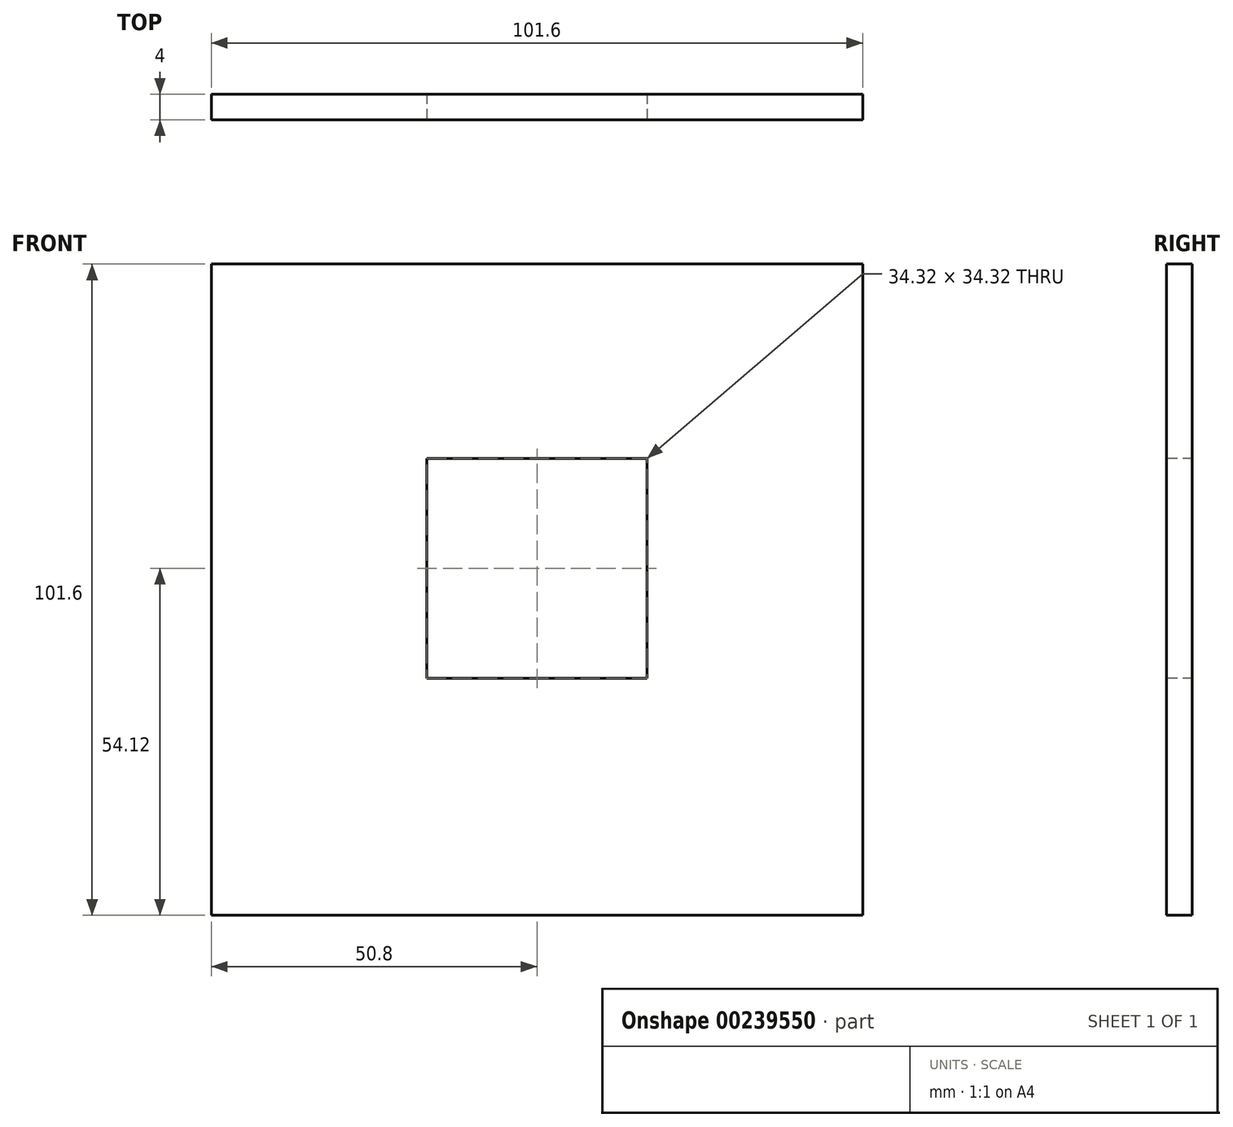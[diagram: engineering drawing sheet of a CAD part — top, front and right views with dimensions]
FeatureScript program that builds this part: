
annotation { "Feature Type Name" : "Feature", "Feature Type Description" : "" }
export const myFeature = defineFeature(function(context is Context, id is Id, definition is map)
    precondition{}
    {
        {
            assignVariable(context, id + "F0", {"name" : "L", "anyValue" : 4});
        }
        {
            var Q0;
            Q0=qCreatedBy(makeId("Front.planeOp"),FACE);
            var sketch = newSketch(context, id + "F1", { "sketchPlane" : qUnion([Q0])});
            skLineSegment(sketch, "E0.bottom", {"start": v(50.8, 50.8) * mm, "end": v(-50.8, 50.8) * mm});
            skLineSegment(sketch, "E0.top", {"start": v(50.8, -50.8) * mm, "end": v(-50.8, -50.8) * mm});
            skLineSegment(sketch, "E0.left", {"start": v(50.8, 50.8) * mm, "end": v(50.8, -50.8) * mm});
            skLineSegment(sketch, "E0.right", {"start": v(-50.8, 50.8) * mm, "end": v(-50.8, -50.8) * mm});
            skPoint(sketch, "E0.middle", {"position": v(0, 0) * mm});
            skSolve(sketch);
        }
        {
            var Q0;
            Q0=makeQuery(id+"F1.imprint","IMPRINT",FACE,{"disambiguationData":[TD([[makeQuery(id+"F1.imprint","IMPRINT",EDGE,{"derivedFrom":sQuery(id+"F1.wireOp",EDGE,"E0.bottom")}),1.0]])]});
            extrude(context, id + "F2", {"entities" : qUnion([Q0]), "endBound" : BoundingType.SYMMETRIC, "depth" : (getVariable(context, 'L')) * mm});
        }
        {
            var Q0;
            Q0=makeQuery(id+"F2.opExtrude","CAP_FACE",FACE,{"disambiguationData":[OSD([sQuery(id+"F1.wireOp",EDGE,"E0.bottom"),sQuery(id+"F1.wireOp",EDGE,"E0.top"),sQuery(id+"F1.wireOp",EDGE,"E0.left"),sQuery(id+"F1.wireOp",EDGE,"E0.right")])],"isStart":false});
            var sketch = newSketch(context, id + "F3", { "sketchPlane" : qUnion([Q0])});
            skLineSegment(sketch, "E1.bottom", {"start": v(17.16, 20.48) * mm, "end": v(-17.16, 20.48) * mm});
            skLineSegment(sketch, "E1.top", {"start": v(17.16, -13.84) * mm, "end": v(-17.16, -13.84) * mm});
            skLineSegment(sketch, "E1.left", {"start": v(17.16, 20.48) * mm, "end": v(17.16, -13.84) * mm});
            skLineSegment(sketch, "E1.right", {"start": v(-17.16, 20.48) * mm, "end": v(-17.16, -13.84) * mm});
            skPoint(sketch, "E1.middle", {"position": v(0, 3.32) * mm});
            skSolve(sketch);
        }
        {
            var Q0;
            Q0 = qSketchRegion(id + "F3", true);
            extrude(context, id + "F4", {"entities" : qUnion([Q0]), "operationType" : NewBodyOperationType.REMOVE, "oppositeDirection" : true, "depth" : 46.23 * mm});
        }
        {
            var Q0;
            Q0=makeQuery(id+"F2.opExtrude","CAP_FACE",FACE,{"disambiguationData":[OSD([sQuery(id+"F1.wireOp",EDGE,"E0.bottom"),sQuery(id+"F1.wireOp",EDGE,"E0.top"),sQuery(id+"F1.wireOp",EDGE,"E0.left"),sQuery(id+"F1.wireOp",EDGE,"E0.right")])],"isStart":true});
            var sketch = newSketch(context, id + "F5", { "sketchPlane" : qUnion([Q0])});
            skLineSegment(sketch, "E2.0", {"start": v(-17.16, 20.48) * mm, "end": v(17.16, 20.48) * mm});
            skLineSegment(sketch, "E3.0", {"start": v(-17.16, 20.48) * mm, "end": v(-17.16, -13.84) * mm});
            skLineSegment(sketch, "E4.0", {"start": v(17.16, 20.48) * mm, "end": v(17.16, -13.84) * mm});
            skLineSegment(sketch, "E5.0", {"start": v(-17.16, -13.84) * mm, "end": v(17.16, -13.84) * mm});
            skSolve(sketch);
        }
        {
            var Q0;
            Q0 = qSketchRegion(id + "F5", true);
            extrude(context, id + "F6", {"entities" : qUnion([Q0]), "operationType" : NewBodyOperationType.REMOVE, "oppositeDirection" : true, "depth" : 45.97 * mm});
        }
    });
